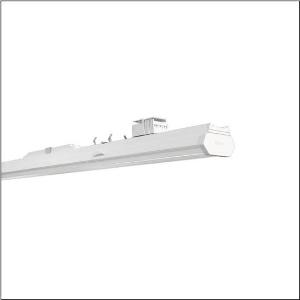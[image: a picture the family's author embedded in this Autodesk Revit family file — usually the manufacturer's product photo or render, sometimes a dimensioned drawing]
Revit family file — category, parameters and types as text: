
# Revit family: licross_r__11_protected_mo_51tp11mn495g_eae0
name_source: partatom
category: Lighting Fixtures
units: mm (PartAtom-declared; Revit-internal decimal feet)

## family parameters
Cut with Voids When Loaded = No
Host = Face
Light Source = No
Part Type = Normal
Room Calculation Point = No
Round Connector Dimension = Use Diameter
Shared = No

## types (1)
- --- (1 x LED, 9980 lm, 55.3 W, 4000K)
    Apparent Load = 55 VA
    CIE Flux Codes = 83 94 98 100 100
    Color Rendering = 80
    Color Temperature = 4000K
    Default Elevation = 1800 mm
    Description = Licross® 11 Protected MO, luminaire insert, of sheet steel, galvanised, coil coated, white, length: 1.500mm, width: 90mm, height: 101mm, LED rated luminous flux: 9.980lm, light colour: 840, control gear: ON/OFF Multilumen, with plug, 3-pole, with phase selection, mains connection: 220..240V, AC, 50/60Hz, rated input power: 55W, halogen-free wiring, primary light control with lens, of plastic, primary optical cover: cover, of PMMA, light emission: direct distribution, primary light characteristic: symmetric, protection rating (complete): IP64, insulation class (complete): insulation class I (protective earthing), certification: CE, ENEC, VDE, UKCA, protection symbol: D if used in an environment with conductive dust loads with corresponding accessories, impact resistance: IK06, permissible ambient temperature for indoor applications: -35..+40°C, corresponds to IFS (International Featured Standards) requirements for safety and quality in the food industry, reducing of maximum allowable ambient temperature of 5°C with ceiling mounting, LABS conformity tested according to VDMA 24364:2018-05, packaging unit: 1 piece
    Height = 92 mm
    Lamp = 1 x LED
    Lamp Light Flux = 9980 lm
    Lamp Power = 55.3 W
    Lamp count = 1
    Length = 1500 mm
    Luminous efficacy = 180 lm/W
    Manufacturer = Siteco
    ModVariant = No
    Model = 51TP11MN495G
    Mounting Place = Ceiling
    Mounting Type = Pendant
    Number of Poles = 1
    OnlyDefault = Yes
    Power Factor = 1
    Product Name = Licross® 11 Protected MO
    Product group = luminaire insert
    ProductGroupID = 901
    Protection Class = Protection class I
    Protection Degree = IP 64
    RLX_Detail_Level = 1
    RLX_Emergency_Light_Flux = 0 lm
    RLX_Emergency_Type = 0
    RLX_Emergency_Type_DB = No
    RlxData = <blob elided: 21801 chars, md5=c2d21f7b>
    Socket = socket
    Standby Power = 0 W
    System Light Flux = 9980 lm
    System Power = 55 W
    Type Comments = factory setting: luminous flux: 100 % | (A | C | E) | 126 mA
    Type Image = l_1256148.jpg
    URL = http://relux.com
    VarID = @adj_055137
    Voltage = 0 V
    Weight = 0.00 kg
    Width = 88 mm

## geometry (parser evidence)
native form markers: Blend x4, Sweep x12
no freeform markers — native parametric forms only
